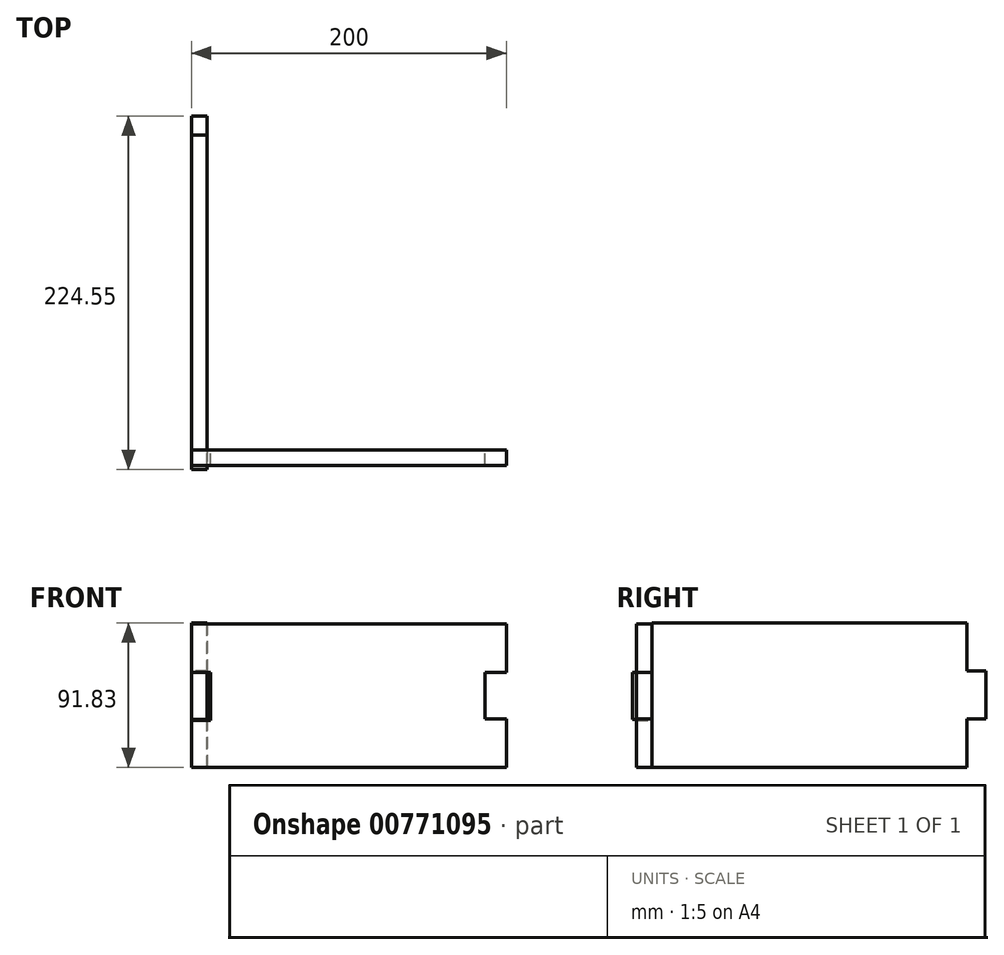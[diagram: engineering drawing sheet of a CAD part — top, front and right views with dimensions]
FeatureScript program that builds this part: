
annotation { "Feature Type Name" : "Feature", "Feature Type Description" : "" }
export const myFeature = defineFeature(function(context is Context, id is Id, definition is map)
    precondition{}
    {
        {
            var Q0;
            Q0=qCreatedBy(makeId("Front.planeOp"),FACE);
            var sketch = newSketch(context, id + "F0", { "sketchPlane" : qUnion([Q0])});
            skLineSegment(sketch, "E0", {"start": v(0, 0) * mm, "end": v(0, 30.1) * mm});
            skLineSegment(sketch, "E1", {"start": v(0, 30.1) * mm, "end": v(12.01, 30.1) * mm});
            skLineSegment(sketch, "E2", {"start": v(12.01, 30.1) * mm, "end": v(12.01, 60.55) * mm});
            skLineSegment(sketch, "E3", {"start": v(0, 0) * mm, "end": v(200, 0) * mm});
            skLineSegment(sketch, "E4", {"start": v(12.01, 60.55) * mm, "end": v(0, 60.55) * mm});
            skLineSegment(sketch, "E5", {"start": v(0, 60.55) * mm, "end": v(0, 91.24) * mm});
            skLineSegment(sketch, "E6", {"start": v(0, 91.24) * mm, "end": v(200, 91.24) * mm});
            skLineSegment(sketch, "E7", {"start": v(200, 91.24) * mm, "end": v(200, 60.55) * mm});
            skLineSegment(sketch, "E8", {"start": v(200, 60.55) * mm, "end": v(186.44, 60.55) * mm});
            skLineSegment(sketch, "E9", {"start": v(186.44, 60.55) * mm, "end": v(186.44, 30.88) * mm});
            skLineSegment(sketch, "E10", {"start": v(186.44, 30.88) * mm, "end": v(200, 30.88) * mm});
            skLineSegment(sketch, "E11", {"start": v(200, 30.88) * mm, "end": v(200, 0) * mm});
            skSolve(sketch);
        }
        {
            var Q0;
            Q0=qCreatedBy(makeId("Right.planeOp"),FACE);
            var sketch = newSketch(context, id + "F1", { "sketchPlane" : qUnion([Q0])});
            skLineSegment(sketch, "E12", {"start": v(0, 0) * mm, "end": v(200, 0) * mm});
            skLineSegment(sketch, "E13", {"start": v(0, 0) * mm, "end": v(0, 30.66) * mm});
            skLineSegment(sketch, "E14", {"start": v(0, 30.66) * mm, "end": v(-12.52, 30.66) * mm});
            skLineSegment(sketch, "E15", {"start": v(-12.52, 30.66) * mm, "end": v(-12.52, 60.46) * mm});
            skLineSegment(sketch, "E16", {"start": v(-12.52, 60.46) * mm, "end": v(0, 60.46) * mm});
            skLineSegment(sketch, "E17", {"start": v(0, 60.46) * mm, "end": v(0, 91.83) * mm});
            skLineSegment(sketch, "E18", {"start": v(0, 91.83) * mm, "end": v(200, 91.83) * mm});
            skLineSegment(sketch, "E19", {"start": v(200, 91.83) * mm, "end": v(200, 61.27) * mm});
            skLineSegment(sketch, "E20", {"start": v(200, 61.27) * mm, "end": v(212.03, 61.27) * mm});
            skLineSegment(sketch, "E21", {"start": v(212.03, 61.27) * mm, "end": v(212.03, 31.01) * mm});
            skLineSegment(sketch, "E22", {"start": v(212.03, 31.01) * mm, "end": v(200, 31.01) * mm});
            skLineSegment(sketch, "E23", {"start": v(200, 31.01) * mm, "end": v(200, 0) * mm});
            skSolve(sketch);
        }
        {
            var Q0;
            Q0 = qSketchRegion(id + "F0", true);
            extrude(context, id + "F2", {"entities" : qUnion([Q0]), "depth" : 10 * mm, "offsetDistance" : 25 * mm});
        }
        {
            var Q0;
            Q0 = qSketchRegion(id + "F1", true);
            extrude(context, id + "F3", {"entities" : qUnion([Q0]), "operationType" : NewBodyOperationType.ADD, "depth" : 10 * mm, "offsetDistance" : 25 * mm});
        }
    });
